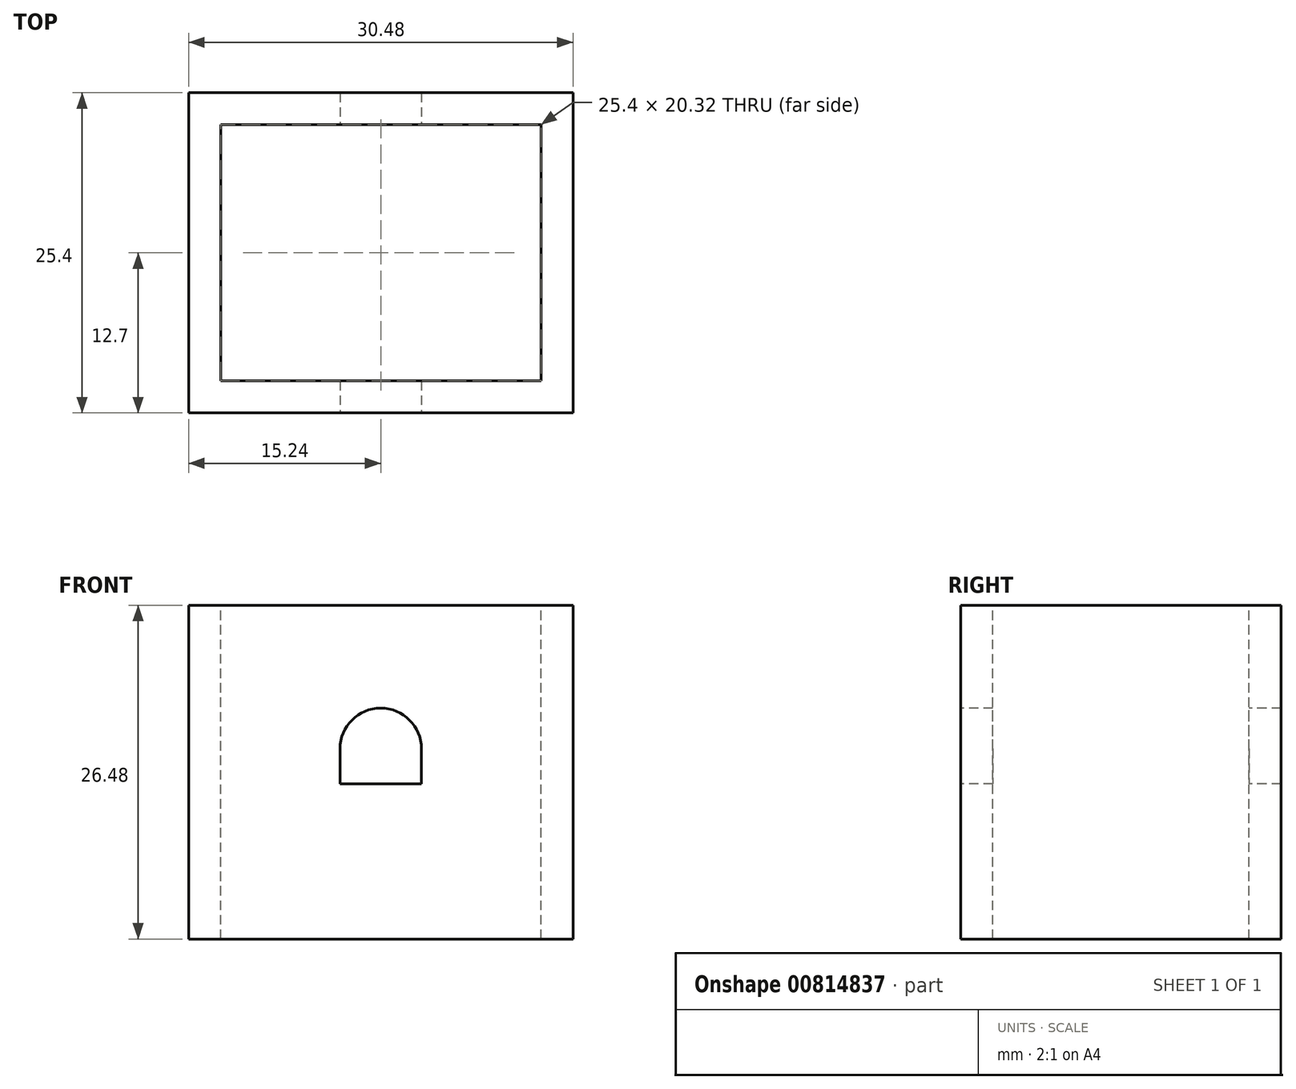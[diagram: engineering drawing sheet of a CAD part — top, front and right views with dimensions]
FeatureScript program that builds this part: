
annotation { "Feature Type Name" : "Feature", "Feature Type Description" : "" }
export const myFeature = defineFeature(function(context is Context, id is Id, definition is map)
    precondition{}
    {
        {
            var Q0;
            Q0=qCreatedBy(makeId("Top.planeOp"),FACE);
            var sketch = newSketch(context, id + "F0", { "sketchPlane" : qUnion([Q0])});
            skLineSegment(sketch, "E0.bottom", {"start": v(-15.24, 12.7) * mm, "end": v(15.24, 12.7) * mm});
            skLineSegment(sketch, "E0.top", {"start": v(-15.24, -12.7) * mm, "end": v(15.24, -12.7) * mm});
            skLineSegment(sketch, "E0.left", {"start": v(-15.24, 12.7) * mm, "end": v(-15.24, -12.7) * mm});
            skLineSegment(sketch, "E0.right", {"start": v(15.24, 12.7) * mm, "end": v(15.24, -12.7) * mm});
            skPoint(sketch, "E0.middle", {"position": v(0, 0) * mm});
            skCircle(sketch, "E1", {"center": v(-6.35, 0) * mm, "radius": 2.16 * mm});
            skCircle(sketch, "E2", {"center": v(6.35, 0) * mm, "radius": 2.16 * mm});
            skLineSegment(sketch, "E3.bottom", {"start": v(-12.7, 10.16) * mm, "end": v(12.7, 10.16) * mm});
            skLineSegment(sketch, "E3.top", {"start": v(-12.7, -10.16) * mm, "end": v(12.7, -10.16) * mm});
            skLineSegment(sketch, "E3.left", {"start": v(-12.7, 10.16) * mm, "end": v(-12.7, -10.16) * mm});
            skLineSegment(sketch, "E3.right", {"start": v(12.7, 10.16) * mm, "end": v(12.7, -10.16) * mm});
            skSolve(sketch);
        }
        {
            var Q0;
            Q0=qSketchRegion(id+"F0",true);
            extrude(context, id + "F1", {"entities" : qUnion([Q0]), "endBound" : BoundingType.SYMMETRIC, "oppositeDirection" : true, "depth" : 88.9 * mm, "offsetDistance" : 25.4 * mm});
        }
        {
            var Q0;
            Q0=makeQuery(id+"F1.opExtrude","CAP_FACE",FACE,{"disambiguationData":[OSD([sQuery(id+"F0.wireOp",EDGE,"E0.bottom"),sQuery(id+"F0.wireOp",EDGE,"E0.top"),sQuery(id+"F0.wireOp",EDGE,"E0.left"),sQuery(id+"F0.wireOp",EDGE,"E0.right"),sQuery(id+"F0.wireOp",EDGE,"E3.bottom"),sQuery(id+"F0.wireOp",EDGE,"E3.top"),sQuery(id+"F0.wireOp",EDGE,"E3.left"),sQuery(id+"F0.wireOp",EDGE,"E3.right")])],"isStart":true});
            var sketch = newSketch(context, id + "F2", { "sketchPlane" : qUnion([Q0])});
            skLineSegment(sketch, "E4.bottom", {"start": v(-12.7, 10.16) * mm, "end": v(12.7, 10.16) * mm});
            skLineSegment(sketch, "E4.top", {"start": v(-12.7, -10.16) * mm, "end": v(12.7, -10.16) * mm});
            skLineSegment(sketch, "E4.left", {"start": v(-12.7, 10.16) * mm, "end": v(-12.7, -10.16) * mm});
            skLineSegment(sketch, "E4.right", {"start": v(12.7, 10.16) * mm, "end": v(12.7, -10.16) * mm});
            skPoint(sketch, "E4.middle", {"position": v(0, 0) * mm});
            skCircle(sketch, "E5", {"center": v(-6.35, 0) * mm, "radius": 2.16 * mm});
            skCircle(sketch, "E6", {"center": v(6.35, 0) * mm, "radius": 2.16 * mm});
            skLineSegment(sketch, "E7.bottom", {"start": v(-10.16, 7.62) * mm, "end": v(10.16, 7.62) * mm});
            skLineSegment(sketch, "E7.top", {"start": v(-10.16, -7.62) * mm, "end": v(10.16, -7.62) * mm});
            skLineSegment(sketch, "E7.left", {"start": v(-10.16, 7.62) * mm, "end": v(-10.16, -7.62) * mm});
            skLineSegment(sketch, "E7.right", {"start": v(10.16, 7.62) * mm, "end": v(10.16, -7.62) * mm});
            skSolve(sketch);
        }
        {
            var Q0;
            Q0=qSketchRegion(id+"F2",true);
            var Q1;
            Q1=makeQuery(id+"F2.imprint","IMPRINT",FACE,{"disambiguationData":[TD([[makeQuery(id+"F2.imprint","IMPRINT",EDGE,{"derivedFrom":sQuery(id+"F2.wireOp",EDGE,"E5")}),-1.0]])]});
            extrude(context, id + "F3", {"entities" : qUnion([Q0, Q1]), "operationType" : NewBodyOperationType.ADD, "oppositeDirection" : true, "depth" : 25.4 * mm, "offsetDistance" : 25.4 * mm});
        }
        {
            var Q0;
            Q0=makeQuery(id+"F3.opExtrude","CAP_FACE",FACE,{"disambiguationData":[OSD([sQuery(id+"F2.wireOp",EDGE,"E4.bottom"),sQuery(id+"F2.wireOp",EDGE,"E4.top"),sQuery(id+"F2.wireOp",EDGE,"E4.left"),sQuery(id+"F2.wireOp",EDGE,"E4.right"),sQuery(id+"F2.wireOp",EDGE,"E5"),sQuery(id+"F2.wireOp",EDGE,"E6")])],"isStart":false});
            var sketch = newSketch(context, id + "F4", { "sketchPlane" : qUnion([Q0])});
            skCircle(sketch, "E8.0", {"center": v(-6.35, 0) * mm, "radius": 2.16 * mm});
            skCircle(sketch, "E9.0", {"center": v(6.35, 0) * mm, "radius": 2.16 * mm});
            skCircle(sketch, "E10", {"center": v(-6.35, 0) * mm, "radius": 5.33 * mm, "construction": true});
            skLineSegment(sketch, "E11.0", {"start": v(-9.02, 4.62) * mm, "end": v(-3.68, 4.62) * mm});
            skLineSegment(sketch, "E11.1", {"start": v(-3.68, 4.62) * mm, "end": v(-1.02, 0) * mm});
            skLineSegment(sketch, "E11.2", {"start": v(-1.02, 0) * mm, "end": v(-3.68, -4.62) * mm});
            skLineSegment(sketch, "E11.3", {"start": v(-3.68, -4.62) * mm, "end": v(-9.02, -4.62) * mm});
            skLineSegment(sketch, "E11.4", {"start": v(-9.02, -4.62) * mm, "end": v(-11.68, 0) * mm});
            skLineSegment(sketch, "E11.5", {"start": v(-11.68, 0) * mm, "end": v(-9.02, 4.62) * mm});
            skCircle(sketch, "E12", {"center": v(6.35, 0) * mm, "radius": 5.33 * mm, "construction": true});
            skLineSegment(sketch, "E13.0", {"start": v(3.68, 4.62) * mm, "end": v(9.02, 4.62) * mm});
            skLineSegment(sketch, "E13.1", {"start": v(9.02, 4.62) * mm, "end": v(11.68, 0) * mm});
            skLineSegment(sketch, "E13.2", {"start": v(11.68, 0) * mm, "end": v(9.02, -4.62) * mm});
            skLineSegment(sketch, "E13.3", {"start": v(9.02, -4.62) * mm, "end": v(3.68, -4.62) * mm});
            skLineSegment(sketch, "E13.4", {"start": v(3.68, -4.62) * mm, "end": v(1.02, 0) * mm});
            skLineSegment(sketch, "E13.5", {"start": v(1.02, 0) * mm, "end": v(3.68, 4.62) * mm});
            skSolve(sketch);
        }
        {
            var Q0;
            Q0=makeQuery(id+"F4.imprint","IMPRINT",FACE,{"disambiguationData":[TD([[makeQuery(id+"F4.imprint","IMPRINT",EDGE,{"derivedFrom":sQuery(id+"F4.wireOp",EDGE,"E9.0")}),1.0]])]});
            var Q1;
            Q1=makeQuery(id+"F4.imprint","IMPRINT",FACE,{"disambiguationData":[TD([[makeQuery(id+"F4.imprint","IMPRINT",EDGE,{"derivedFrom":sQuery(id+"F4.wireOp",EDGE,"E8.0")}),1.0]])]});
            extrude(context, id + "F5", {"entities" : qUnion([Q0, Q1]), "operationType" : NewBodyOperationType.REMOVE, "oppositeDirection" : true, "depth" : 5.08 * mm, "offsetDistance" : 25.4 * mm});
        }
        {
            var Q0;
            Q0=makeQuery(id+"F1.opExtrude","SWEPT_FACE",FACE,{"disambiguationData":[OSD([sQuery(id+"F0.wireOp",EDGE,"E0.top")])]});
            var sketch = newSketch(context, id + "F6", { "sketchPlane" : qUnion([Q0])});
            skLineSegment(sketch, "E14", {"start": v(0, 44.45) * mm, "end": v(0, 19.05) * mm, "construction": true});
            skCircle(sketch, "E15", {"center": v(0, 8) * mm, "radius": 3.43 * mm});
            skLineSegment(sketch, "E16.bottom", {"start": v(-4.06, -6.88) * mm, "end": v(4.06, -6.88) * mm});
            skLineSegment(sketch, "E16.top", {"start": v(-4.06, -9.93) * mm, "end": v(4.06, -9.93) * mm});
            skLineSegment(sketch, "E16.left", {"start": v(-4.06, -6.88) * mm, "end": v(-4.06, -9.93) * mm});
            skLineSegment(sketch, "E16.right", {"start": v(4.06, -6.88) * mm, "end": v(4.06, -9.93) * mm});
            skPoint(sketch, "E16.middle", {"position": v(0, -8.4) * mm});
            skLineSegment(sketch, "E17.top", {"start": v(-3.23, -32.16) * mm, "end": v(3.23, -32.16) * mm});
            skLineSegment(sketch, "E17.left", {"start": v(-3.23, -29.36) * mm, "end": v(-3.23, -32.16) * mm});
            skLineSegment(sketch, "E17.right", {"start": v(3.23, -29.36) * mm, "end": v(3.23, -32.16) * mm});
            skPoint(sketch, "E17.middle", {"position": v(0, -30.76) * mm});
            skArc(sketch, "E18", {"start": v(3.23, -29.36) * mm, "mid": v(0, -26.14) * mm, "end": v(-3.23, -29.36) * mm});
            skLineSegment(sketch, "E19", {"start": v(3.18, -29.36) * mm, "end": v(-3.17, -29.36) * mm, "construction": true});
            skSolve(sketch);
        }
        {
            var Q0;
            Q0 = qSketchRegion(id + "F6", true);
            extrude(context, id + "F7", {"entities" : qUnion([Q0]), "operationType" : NewBodyOperationType.REMOVE, "oppositeDirection" : true, "depth" : 25.4 * mm, "offsetDistance" : 25.4 * mm});
        }
        {
            var Q0;
            Q0=qCreatedBy(makeId("Front.planeOp"),FACE);
            var sketch = newSketch(context, id + "F8", { "sketchPlane" : qUnion([Q0])});
            skLineSegment(sketch, "E20.bottom", {"start": v(-24.98, 50.97) * mm, "end": v(29.22, 50.97) * mm});
            skLineSegment(sketch, "E20.top", {"start": v(-24.98, -17.97) * mm, "end": v(29.22, -17.97) * mm});
            skLineSegment(sketch, "E20.left", {"start": v(-24.98, 50.97) * mm, "end": v(-24.98, -17.97) * mm});
            skLineSegment(sketch, "E20.right", {"start": v(29.22, 50.97) * mm, "end": v(29.22, -17.97) * mm});
            skSolve(sketch);
        }
        {
            var Q0;
            Q0 = qSketchRegion(id + "F8", true);
            extrude(context, id + "F9", {"entities" : qUnion([Q0]), "operationType" : NewBodyOperationType.REMOVE, "endBound" : BoundingType.SYMMETRIC, "oppositeDirection" : true, "depth" : 25.4 * mm, "offsetDistance" : 25.4 * mm});
        }
    });
